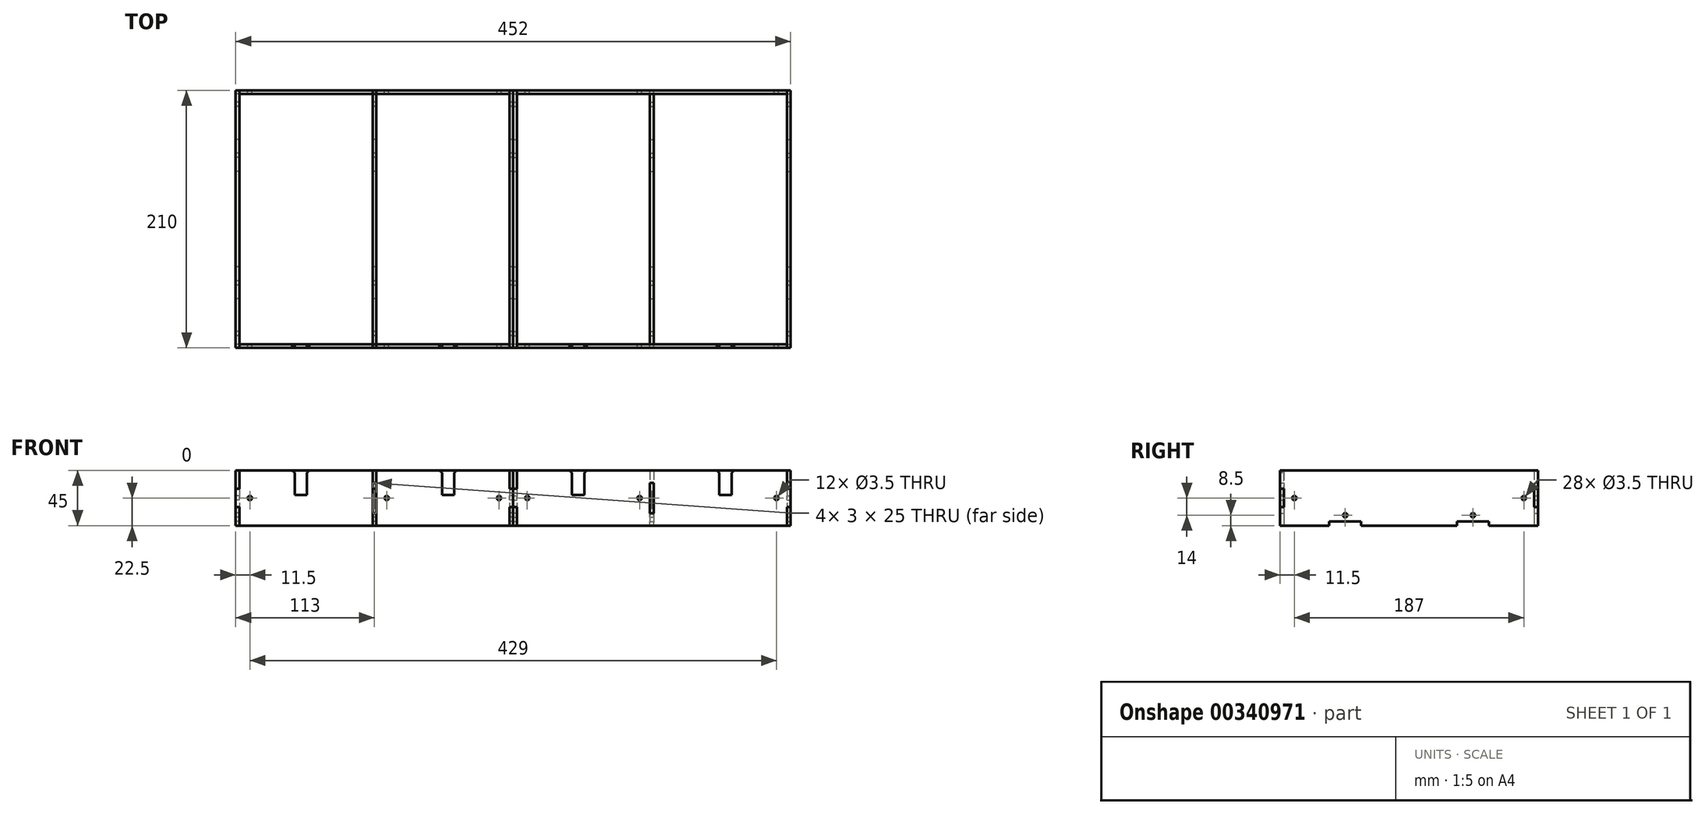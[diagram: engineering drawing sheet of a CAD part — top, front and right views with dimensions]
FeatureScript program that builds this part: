
annotation { "Feature Type Name" : "Feature", "Feature Type Description" : "" }
export const myFeature = defineFeature(function(context is Context, id is Id, definition is map)
    precondition{}
    {
        {
            var Q0;
            Q0=qCreatedBy(makeId("Right.planeOp"),FACE);
            var sketch = newSketch(context, id + "F0", { "sketchPlane" : qUnion([Q0])});
            skLineSegment(sketch, "E0.bottom", {"start": v(-105, 0) * mm, "end": v(-65, 0) * mm});
            skLineSegment(sketch, "E0.top", {"start": v(-105, 45) * mm, "end": v(105, 45) * mm});
            skLineSegment(sketch, "E0.left", {"start": v(-105, 0) * mm, "end": v(-105, 15) * mm});
            skLineSegment(sketch, "E0.right", {"start": v(105, 0) * mm, "end": v(105, 15) * mm});
            skPoint(sketch, "E0.middle", {"position": v(0, 22.5) * mm});
            skCircle(sketch, "E1", {"center": v(-93.5, 22.5) * mm, "radius": 1.75 * mm});
            skPoint(sketch, "E1.centerSnap0", {"position": v(-105, 22.5) * mm});
            skCircle(sketch, "E2", {"center": v(-52, 8.5) * mm, "radius": 1.75 * mm});
            skLineSegment(sketch, "E3.top", {"start": v(-65, 3.5) * mm, "end": v(-39, 3.5) * mm});
            skLineSegment(sketch, "E3.left", {"start": v(-65, 0) * mm, "end": v(-65, 3.5) * mm});
            skLineSegment(sketch, "E3.right", {"start": v(-39, 0) * mm, "end": v(-39, 3.5) * mm});
            skPoint(sketch, "E4", {"position": v(-52, 3.5) * mm});
            skLineSegment(sketch, "E5.bottom", {"start": v(-105, 30) * mm, "end": v(-102, 30) * mm});
            skLineSegment(sketch, "E5.top", {"start": v(-105, 15) * mm, "end": v(-102, 15) * mm});
            skLineSegment(sketch, "E5.right", {"start": v(-102, 30) * mm, "end": v(-102, 15) * mm});
            skPoint(sketch, "E5.middle", {"position": v(-103.5, 22.5) * mm});
            skLineSegment(sketch, "E6.trimOffspring", {"start": v(-105, 30) * mm, "end": v(-105, 45) * mm});
            skLineSegment(sketch, "E7.trimOffspring", {"start": v(-39, 0) * mm, "end": v(39, 0) * mm});
            skLineSegment(sketch, "E8.MirrorCS", {"start": v(39, 0) * mm, "end": v(39, 3.5) * mm});
            skLineSegment(sketch, "E9.MirrorCS", {"start": v(65, 0) * mm, "end": v(65, 3.5) * mm});
            skLineSegment(sketch, "E10.MirrorCS", {"start": v(105, 15) * mm, "end": v(102, 15) * mm});
            skLineSegment(sketch, "E11.MirrorCS", {"start": v(105, 30) * mm, "end": v(102, 30) * mm});
            skCircle(sketch, "E12.MirrorC", {"center": v(93.5, 22.5) * mm, "radius": 1.75 * mm});
            skPoint(sketch, "E13.MirrorP", {"position": v(103.5, 22.5) * mm});
            skLineSegment(sketch, "E14.MirrorCS", {"start": v(105, 0) * mm, "end": v(65, 0) * mm});
            skLineSegment(sketch, "E15.MirrorCS", {"start": v(39, 0) * mm, "end": v(-39, 0) * mm});
            skPoint(sketch, "E16.MirrorP", {"position": v(105, 22.5) * mm});
            skPoint(sketch, "E17.MirrorP", {"position": v(52, 3.5) * mm});
            skLineSegment(sketch, "E18.MirrorCS", {"start": v(105, 30) * mm, "end": v(105, 45) * mm});
            skLineSegment(sketch, "E19.MirrorCS", {"start": v(102, 30) * mm, "end": v(102, 15) * mm});
            skLineSegment(sketch, "E20.MirrorCS", {"start": v(65, 3.5) * mm, "end": v(39, 3.5) * mm});
            skCircle(sketch, "E21.MirrorC", {"center": v(52, 8.5) * mm, "radius": 1.75 * mm});
            skLineSegment(sketch, "E22.trimOffspring", {"start": v(65, 0) * mm, "end": v(105, 0) * mm});
            skLineSegment(sketch, "E23.trimOffspring", {"start": v(-65, 0) * mm, "end": v(-105, 0) * mm});
            skSolve(sketch);
        }
        {
            var Q0;
            Q0 = qSketchRegion(id + "F0", true);
            extrude(context, id + "F1", {"entities" : qUnion([Q0]), "depth" : 1.5 * mm, "hasSecondDirection" : true, "secondDirectionOppositeDirection" : true, "secondDirectionDepth" : 1.5 * mm});
        }
        {
            var Q0;
            Q0=makeQuery(id+"F1.opExtrude","SWEPT_BODY",BODY,{"disambiguationData":[OSD([sQuery(id+"F0.wireOp",EDGE,"E0.top"),sQuery(id+"F0.wireOp",EDGE,"E0.left"),sQuery(id+"F0.wireOp",EDGE,"E1"),sQuery(id+"F0.wireOp",EDGE,"E2"),sQuery(id+"F0.wireOp",EDGE,"E3.top"),sQuery(id+"F0.wireOp",EDGE,"E3.left"),sQuery(id+"F0.wireOp",EDGE,"E3.right"),sQuery(id+"F0.wireOp",EDGE,"E5.bottom"),sQuery(id+"F0.wireOp",EDGE,"E5.top"),sQuery(id+"F0.wireOp",EDGE,"E5.right"),sQuery(id+"F0.wireOp",EDGE,"E6.trimOffspring"),sQuery(id+"F0.wireOp",EDGE,"E8.MirrorCS"),sQuery(id+"F0.wireOp",EDGE,"E9.MirrorCS"),sQuery(id+"F0.wireOp",EDGE,"E10.MirrorCS"),sQuery(id+"F0.wireOp",EDGE,"E11.MirrorCS"),sQuery(id+"F0.wireOp",EDGE,"E12.MirrorC"),sQuery(id+"F0.wireOp",EDGE,"E0.right"),sQuery(id+"F0.wireOp",EDGE,"E15.MirrorCS"),sQuery(id+"F0.wireOp",EDGE,"E19.MirrorCS"),sQuery(id+"F0.wireOp",EDGE,"E20.MirrorCS"),sQuery(id+"F0.wireOp",EDGE,"E21.MirrorC"),sQuery(id+"F0.wireOp",EDGE,"E18.MirrorCS"),sQuery(id+"F0.wireOp",EDGE,"E22.trimOffspring"),sQuery(id+"F0.wireOp",EDGE,"E23.trimOffspring")])]});
            transform(context, id + "F2", {"entities" : qUnion([Q0]), "transformType" : TransformType.TRANSLATION_3D, "dx" : (223 / 2) * mm, "dy" : 0 * mm, "dz" : 0 * mm, "makeCopy" : true});
        }
        {
            var Q0;
            Q0=makeQuery(id+"F1.opExtrude","SWEPT_BODY",BODY,{"disambiguationData":[OSD([sQuery(id+"F0.wireOp",EDGE,"E0.top"),sQuery(id+"F0.wireOp",EDGE,"E0.left"),sQuery(id+"F0.wireOp",EDGE,"E1"),sQuery(id+"F0.wireOp",EDGE,"E2"),sQuery(id+"F0.wireOp",EDGE,"E3.top"),sQuery(id+"F0.wireOp",EDGE,"E3.left"),sQuery(id+"F0.wireOp",EDGE,"E3.right"),sQuery(id+"F0.wireOp",EDGE,"E5.bottom"),sQuery(id+"F0.wireOp",EDGE,"E5.top"),sQuery(id+"F0.wireOp",EDGE,"E5.right"),sQuery(id+"F0.wireOp",EDGE,"E6.trimOffspring"),sQuery(id+"F0.wireOp",EDGE,"E8.MirrorCS"),sQuery(id+"F0.wireOp",EDGE,"E9.MirrorCS"),sQuery(id+"F0.wireOp",EDGE,"E10.MirrorCS"),sQuery(id+"F0.wireOp",EDGE,"E11.MirrorCS"),sQuery(id+"F0.wireOp",EDGE,"E12.MirrorC"),sQuery(id+"F0.wireOp",EDGE,"E0.right"),sQuery(id+"F0.wireOp",EDGE,"E15.MirrorCS"),sQuery(id+"F0.wireOp",EDGE,"E19.MirrorCS"),sQuery(id+"F0.wireOp",EDGE,"E20.MirrorCS"),sQuery(id+"F0.wireOp",EDGE,"E21.MirrorC"),sQuery(id+"F0.wireOp",EDGE,"E18.MirrorCS"),sQuery(id+"F0.wireOp",EDGE,"E22.trimOffspring"),sQuery(id+"F0.wireOp",EDGE,"E23.trimOffspring")])]});
            transform(context, id + "F3", {"entities" : qUnion([Q0]), "transformType" : TransformType.TRANSLATION_3D, "dx" : (-(223 / 2)) * mm, "dy" : 0 * mm, "dz" : 0 * mm, "makeCopy" : true});
        }
        {
            var Q0;
            Q0=makeQuery(id+"F1.opExtrude","SWEPT_BODY",BODY,{"disambiguationData":[OSD([sQuery(id+"F0.wireOp",EDGE,"E0.top"),sQuery(id+"F0.wireOp",EDGE,"E0.left"),sQuery(id+"F0.wireOp",EDGE,"E1"),sQuery(id+"F0.wireOp",EDGE,"E2"),sQuery(id+"F0.wireOp",EDGE,"E3.top"),sQuery(id+"F0.wireOp",EDGE,"E3.left"),sQuery(id+"F0.wireOp",EDGE,"E3.right"),sQuery(id+"F0.wireOp",EDGE,"E5.bottom"),sQuery(id+"F0.wireOp",EDGE,"E5.top"),sQuery(id+"F0.wireOp",EDGE,"E5.right"),sQuery(id+"F0.wireOp",EDGE,"E6.trimOffspring"),sQuery(id+"F0.wireOp",EDGE,"E8.MirrorCS"),sQuery(id+"F0.wireOp",EDGE,"E9.MirrorCS"),sQuery(id+"F0.wireOp",EDGE,"E10.MirrorCS"),sQuery(id+"F0.wireOp",EDGE,"E11.MirrorCS"),sQuery(id+"F0.wireOp",EDGE,"E12.MirrorC"),sQuery(id+"F0.wireOp",EDGE,"E0.right"),sQuery(id+"F0.wireOp",EDGE,"E15.MirrorCS"),sQuery(id+"F0.wireOp",EDGE,"E19.MirrorCS"),sQuery(id+"F0.wireOp",EDGE,"E20.MirrorCS"),sQuery(id+"F0.wireOp",EDGE,"E21.MirrorC"),sQuery(id+"F0.wireOp",EDGE,"E18.MirrorCS"),sQuery(id+"F0.wireOp",EDGE,"E22.trimOffspring"),sQuery(id+"F0.wireOp",EDGE,"E23.trimOffspring")])]});
            transform(context, id + "F4", {"entities" : qUnion([Q0]), "transformType" : TransformType.TRANSLATION_3D, "dx" : 0 * mm, "dy" : 0 * mm, "dz" : 0 * mm, "makeCopy" : true});
        }
        {
            var Q0;
            Q0=makeQuery(id+"F4.opPattern","COPY",BODY,{"derivedFrom":makeQuery(id+"F1.opExtrude","SWEPT_BODY",BODY,{"disambiguationData":[OSD([sQuery(id+"F0.wireOp",EDGE,"E0.top"),sQuery(id+"F0.wireOp",EDGE,"E0.left"),sQuery(id+"F0.wireOp",EDGE,"E1"),sQuery(id+"F0.wireOp",EDGE,"E2"),sQuery(id+"F0.wireOp",EDGE,"E3.top"),sQuery(id+"F0.wireOp",EDGE,"E3.left"),sQuery(id+"F0.wireOp",EDGE,"E3.right"),sQuery(id+"F0.wireOp",EDGE,"E5.bottom"),sQuery(id+"F0.wireOp",EDGE,"E5.top"),sQuery(id+"F0.wireOp",EDGE,"E5.right"),sQuery(id+"F0.wireOp",EDGE,"E6.trimOffspring"),sQuery(id+"F0.wireOp",EDGE,"E8.MirrorCS"),sQuery(id+"F0.wireOp",EDGE,"E9.MirrorCS"),sQuery(id+"F0.wireOp",EDGE,"E10.MirrorCS"),sQuery(id+"F0.wireOp",EDGE,"E11.MirrorCS"),sQuery(id+"F0.wireOp",EDGE,"E12.MirrorC"),sQuery(id+"F0.wireOp",EDGE,"E0.right"),sQuery(id+"F0.wireOp",EDGE,"E15.MirrorCS"),sQuery(id+"F0.wireOp",EDGE,"E19.MirrorCS"),sQuery(id+"F0.wireOp",EDGE,"E20.MirrorCS"),sQuery(id+"F0.wireOp",EDGE,"E21.MirrorC"),sQuery(id+"F0.wireOp",EDGE,"E18.MirrorCS"),sQuery(id+"F0.wireOp",EDGE,"E22.trimOffspring"),sQuery(id+"F0.wireOp",EDGE,"E23.trimOffspring")])]}),"instanceName":"1"});
            deleteBodies(context, id + "F5", {"entities" : qUnion([Q0])});
        }
        {
            var Q0;
            Q0=qCreatedBy(makeId("Right.planeOp"),FACE);
            var sketch = newSketch(context, id + "F6", { "sketchPlane" : qUnion([Q0])});
            skLineSegment(sketch, "E24.bottom", {"start": v(-102, 0) * mm, "end": v(-65, 0) * mm});
            skLineSegment(sketch, "E24.top", {"start": v(-102, 45) * mm, "end": v(102, 45) * mm});
            skLineSegment(sketch, "E24.left", {"start": v(-105, 10) * mm, "end": v(-105, 35) * mm});
            skCircle(sketch, "E25", {"center": v(-93.5, 22.5) * mm, "radius": 1.75 * mm});
            skCircle(sketch, "E26", {"center": v(-52, 8.5) * mm, "radius": 1.75 * mm});
            skLineSegment(sketch, "E27.top", {"start": v(-65, 3.5) * mm, "end": v(-39, 3.5) * mm});
            skLineSegment(sketch, "E27.left", {"start": v(-65, 0) * mm, "end": v(-65, 3.5) * mm});
            skLineSegment(sketch, "E27.right", {"start": v(-39, 0) * mm, "end": v(-39, 3.5) * mm});
            skPoint(sketch, "E28", {"position": v(-52, 3.5) * mm});
            skLineSegment(sketch, "E29.trimOffspring", {"start": v(-39, 0) * mm, "end": v(39, 0) * mm});
            skLineSegment(sketch, "E30.MirrorCS", {"start": v(39, 0) * mm, "end": v(39, 3.5) * mm});
            skLineSegment(sketch, "E31.MirrorCS", {"start": v(65, 0) * mm, "end": v(65, 3.5) * mm});
            skCircle(sketch, "E32.MirrorC", {"center": v(93.5, 22.5) * mm, "radius": 1.75 * mm});
            skLineSegment(sketch, "E33.MirrorCS", {"start": v(102, 0) * mm, "end": v(65, 0) * mm});
            skLineSegment(sketch, "E34.MirrorCS", {"start": v(39, 0) * mm, "end": v(-39, 0) * mm});
            skPoint(sketch, "E35.MirrorP", {"position": v(52, 3.5) * mm});
            skLineSegment(sketch, "E36.MirrorCS", {"start": v(65, 3.5) * mm, "end": v(39, 3.5) * mm});
            skCircle(sketch, "E37.MirrorC", {"center": v(52, 8.5) * mm, "radius": 1.75 * mm});
            skLineSegment(sketch, "E38.trimOffspring", {"start": v(65, 0) * mm, "end": v(102, 0) * mm});
            skLineSegment(sketch, "E39.trimOffspring", {"start": v(-65, 0) * mm, "end": v(-102, 0) * mm});
            skLineSegment(sketch, "E40", {"start": v(-102, 45) * mm, "end": v(-102, 35) * mm});
            skLineSegment(sketch, "E41", {"start": v(-102, 35) * mm, "end": v(-105, 35) * mm});
            skLineSegment(sketch, "E42", {"start": v(-105, 10) * mm, "end": v(-102, 10) * mm});
            skLineSegment(sketch, "E43", {"start": v(-102, 10) * mm, "end": v(-102, 0) * mm});
            skLineSegment(sketch, "E44.MirrorCS", {"start": v(102, 45) * mm, "end": v(102, 35) * mm});
            skLineSegment(sketch, "E45.MirrorCS", {"start": v(102, 35) * mm, "end": v(105, 35) * mm});
            skLineSegment(sketch, "E46.MirrorCS", {"start": v(105, 35) * mm, "end": v(105, 10) * mm});
            skLineSegment(sketch, "E47.MirrorCS", {"start": v(105, 10) * mm, "end": v(102, 10) * mm});
            skLineSegment(sketch, "E48.MirrorCS", {"start": v(102, 10) * mm, "end": v(102, 0) * mm});
            skPoint(sketch, "E49", {"position": v(-105, 22.5) * mm});
            skSolve(sketch);
        }
        {
            var Q0;
            Q0 = qSketchRegion(id + "F6", true);
            extrude(context, id + "F7", {"entities" : qUnion([Q0]), "depth" : 1.5 * mm, "hasSecondDirection" : true, "secondDirectionOppositeDirection" : true, "secondDirectionDepth" : 1.5 * mm});
        }
        {
            var Q0;
            Q0=makeQuery(id+"F7.opExtrude","SWEPT_FACE",FACE,{"disambiguationData":[OSD([sQuery(id+"F6.wireOp",EDGE,"E40")])]});
            var sketch = newSketch(context, id + "F8", { "sketchPlane" : qUnion([Q0])});
            skLineSegment(sketch, "E50", {"start": v(110, 45) * mm, "end": v(-110, 45) * mm});
            skLineSegment(sketch, "E51", {"start": v(-110, 45) * mm, "end": v(-110, 30) * mm});
            skLineSegment(sketch, "E52", {"start": v(-110, 30) * mm, "end": v(-113, 30) * mm});
            skLineSegment(sketch, "E53", {"start": v(-113, 30) * mm, "end": v(-113, 15) * mm});
            skLineSegment(sketch, "E54", {"start": v(-113, 15) * mm, "end": v(-110, 15) * mm});
            skLineSegment(sketch, "E55", {"start": v(-110, 15) * mm, "end": v(-110, 0) * mm});
            skLineSegment(sketch, "E56", {"start": v(-110, 0) * mm, "end": v(110, 0) * mm});
            skLineSegment(sketch, "E57", {"start": v(110, 0) * mm, "end": v(110, 15) * mm});
            skLineSegment(sketch, "E58", {"start": v(110, 15) * mm, "end": v(113, 15) * mm});
            skLineSegment(sketch, "E59", {"start": v(113, 15) * mm, "end": v(113, 30) * mm});
            skLineSegment(sketch, "E60", {"start": v(113, 30) * mm, "end": v(110, 30) * mm});
            skLineSegment(sketch, "E61", {"start": v(110, 30) * mm, "end": v(110, 45) * mm});
            skLineSegment(sketch, "E62.bottom", {"start": v(-1.5, 35) * mm, "end": v(1.5, 35) * mm});
            skLineSegment(sketch, "E62.top", {"start": v(-1.5, 10) * mm, "end": v(1.5, 10) * mm});
            skLineSegment(sketch, "E62.left", {"start": v(-1.5, 35) * mm, "end": v(-1.5, 10) * mm});
            skLineSegment(sketch, "E62.right", {"start": v(1.5, 35) * mm, "end": v(1.5, 10) * mm});
            skPoint(sketch, "E63", {"position": v(-113, 22.5) * mm});
            skCircle(sketch, "E64", {"center": v(-101.5, 22.5) * mm, "radius": 1.75 * mm});
            skCircle(sketch, "E65", {"center": v(10, 22.5) * mm, "radius": 1.75 * mm});
            skCircle(sketch, "E66.MirrorC", {"center": v(101.5, 22.5) * mm, "radius": 1.75 * mm});
            skSolve(sketch);
        }
        {
            var Q0;
            Q0 = qSketchRegion(id + "F8", true);
            extrude(context, id + "F9", {"entities" : qUnion([Q0]), "depth" : 3 * mm});
        }
        {
            var Q0;
            Q0=makeQuery(id+"F9.opExtrude","SWEPT_BODY",BODY,{"disambiguationData":[OSD([sQuery(id+"F8.wireOp",EDGE,"E50"),sQuery(id+"F8.wireOp",EDGE,"E51"),sQuery(id+"F8.wireOp",EDGE,"E52"),sQuery(id+"F8.wireOp",EDGE,"E53"),sQuery(id+"F8.wireOp",EDGE,"E54"),sQuery(id+"F8.wireOp",EDGE,"E55"),sQuery(id+"F8.wireOp",EDGE,"E56"),sQuery(id+"F8.wireOp",EDGE,"E57"),sQuery(id+"F8.wireOp",EDGE,"E58"),sQuery(id+"F8.wireOp",EDGE,"E59"),sQuery(id+"F8.wireOp",EDGE,"E60"),sQuery(id+"F8.wireOp",EDGE,"E61"),sQuery(id+"F8.wireOp",EDGE,"E62.bottom"),sQuery(id+"F8.wireOp",EDGE,"E62.top"),sQuery(id+"F8.wireOp",EDGE,"E62.left"),sQuery(id+"F8.wireOp",EDGE,"E62.right"),sQuery(id+"F8.wireOp",EDGE,"E64"),sQuery(id+"F8.wireOp",EDGE,"E65"),sQuery(id+"F8.wireOp",EDGE,"E66.MirrorC")])]});
            transform(context, id + "F10", {"entities" : qUnion([Q0]), "transformType" : TransformType.TRANSLATION_3D, "dx" : 0 * mm, "dy" : (210 - 3) * mm, "dz" : 0 * mm, "makeCopy" : true});
        }
        {
            var Q0;
            Q0=makeQuery(id+"F9.opExtrude","CAP_FACE",FACE,{"disambiguationData":[OSD([sQuery(id+"F8.wireOp",EDGE,"E50"),sQuery(id+"F8.wireOp",EDGE,"E51"),sQuery(id+"F8.wireOp",EDGE,"E52"),sQuery(id+"F8.wireOp",EDGE,"E53"),sQuery(id+"F8.wireOp",EDGE,"E54"),sQuery(id+"F8.wireOp",EDGE,"E55"),sQuery(id+"F8.wireOp",EDGE,"E56"),sQuery(id+"F8.wireOp",EDGE,"E57"),sQuery(id+"F8.wireOp",EDGE,"E58"),sQuery(id+"F8.wireOp",EDGE,"E59"),sQuery(id+"F8.wireOp",EDGE,"E60"),sQuery(id+"F8.wireOp",EDGE,"E61"),sQuery(id+"F8.wireOp",EDGE,"E62.bottom"),sQuery(id+"F8.wireOp",EDGE,"E62.top"),sQuery(id+"F8.wireOp",EDGE,"E62.left"),sQuery(id+"F8.wireOp",EDGE,"E62.right"),sQuery(id+"F8.wireOp",EDGE,"E64"),sQuery(id+"F8.wireOp",EDGE,"E65"),sQuery(id+"F8.wireOp",EDGE,"E66.MirrorC")])],"isStart":false});
            var sketch = newSketch(context, id + "F11", { "sketchPlane" : qUnion([Q0])});
            skLineSegment(sketch, "E67.bottom", {"start": v(-65, 45) * mm, "end": v(-55, 45) * mm});
            skLineSegment(sketch, "E67.top", {"start": v(-65, 25) * mm, "end": v(-55, 25) * mm});
            skLineSegment(sketch, "E67.left", {"start": v(-65, 43) * mm, "end": v(-65, 25) * mm});
            skLineSegment(sketch, "E67.right", {"start": v(-55, 43) * mm, "end": v(-55, 25) * mm});
            skLineSegment(sketch, "E68", {"start": v(-65, 43) * mm, "end": v(-67, 45) * mm});
            skLineSegment(sketch, "E69", {"start": v(-67, 45) * mm, "end": v(-53, 45) * mm});
            skLineSegment(sketch, "E70", {"start": v(-53, 45) * mm, "end": v(-55, 43) * mm});
            skPoint(sketch, "E71", {"position": v(-60, 45) * mm});
            skLineSegment(sketch, "E72", {"start": v(-60, 45) * mm, "end": v(-60, 25) * mm, "construction": true});
            skLineSegment(sketch, "E73.MirrorCS", {"start": v(65, 45) * mm, "end": v(55, 45) * mm});
            skLineSegment(sketch, "E74.MirrorCS", {"start": v(53, 45) * mm, "end": v(55, 43) * mm});
            skLineSegment(sketch, "E75.MirrorCS", {"start": v(65, 43) * mm, "end": v(67, 45) * mm});
            skLineSegment(sketch, "E76.MirrorCS", {"start": v(67, 45) * mm, "end": v(53, 45) * mm});
            skLineSegment(sketch, "E77.MirrorCS", {"start": v(65, 25) * mm, "end": v(55, 25) * mm});
            skLineSegment(sketch, "E78.MirrorCS", {"start": v(65, 43) * mm, "end": v(65, 25) * mm});
            skPoint(sketch, "E79.MirrorP", {"position": v(60, 45) * mm});
            skLineSegment(sketch, "E80.MirrorCS", {"start": v(60, 45) * mm, "end": v(60, 25) * mm, "construction": true});
            skLineSegment(sketch, "E81.MirrorCS", {"start": v(55, 43) * mm, "end": v(55, 25) * mm});
            skSolve(sketch);
        }
        {
            var Q0;
            Q0 = qSketchRegion(id + "F11", true);
            extrude(context, id + "F12", {"entities" : qUnion([Q0]), "operationType" : NewBodyOperationType.REMOVE, "endBound" : BoundingType.UP_TO_NEXT, "oppositeDirection" : true, "depth" : 25 * mm});
        }
        {
            var Q0;
            Q0=makeQuery(id+"F2.opPattern","COPY",BODY,{"derivedFrom":makeQuery(id+"F1.opExtrude","SWEPT_BODY",BODY,{"disambiguationData":[OSD([sQuery(id+"F0.wireOp",EDGE,"E0.top"),sQuery(id+"F0.wireOp",EDGE,"E0.left"),sQuery(id+"F0.wireOp",EDGE,"E1"),sQuery(id+"F0.wireOp",EDGE,"E2"),sQuery(id+"F0.wireOp",EDGE,"E3.top"),sQuery(id+"F0.wireOp",EDGE,"E3.left"),sQuery(id+"F0.wireOp",EDGE,"E3.right"),sQuery(id+"F0.wireOp",EDGE,"E5.bottom"),sQuery(id+"F0.wireOp",EDGE,"E5.top"),sQuery(id+"F0.wireOp",EDGE,"E5.right"),sQuery(id+"F0.wireOp",EDGE,"E6.trimOffspring"),sQuery(id+"F0.wireOp",EDGE,"E8.MirrorCS"),sQuery(id+"F0.wireOp",EDGE,"E9.MirrorCS"),sQuery(id+"F0.wireOp",EDGE,"E10.MirrorCS"),sQuery(id+"F0.wireOp",EDGE,"E11.MirrorCS"),sQuery(id+"F0.wireOp",EDGE,"E12.MirrorC"),sQuery(id+"F0.wireOp",EDGE,"E0.right"),sQuery(id+"F0.wireOp",EDGE,"E15.MirrorCS"),sQuery(id+"F0.wireOp",EDGE,"E19.MirrorCS"),sQuery(id+"F0.wireOp",EDGE,"E20.MirrorCS"),sQuery(id+"F0.wireOp",EDGE,"E21.MirrorC"),sQuery(id+"F0.wireOp",EDGE,"E18.MirrorCS"),sQuery(id+"F0.wireOp",EDGE,"E22.trimOffspring"),sQuery(id+"F0.wireOp",EDGE,"E23.trimOffspring")])]}),"instanceName":"1"});
            var Q1;
            Q1=makeQuery(id+"F3.opPattern","COPY",BODY,{"derivedFrom":makeQuery(id+"F1.opExtrude","SWEPT_BODY",BODY,{"disambiguationData":[OSD([sQuery(id+"F0.wireOp",EDGE,"E0.top"),sQuery(id+"F0.wireOp",EDGE,"E0.left"),sQuery(id+"F0.wireOp",EDGE,"E1"),sQuery(id+"F0.wireOp",EDGE,"E2"),sQuery(id+"F0.wireOp",EDGE,"E3.top"),sQuery(id+"F0.wireOp",EDGE,"E3.left"),sQuery(id+"F0.wireOp",EDGE,"E3.right"),sQuery(id+"F0.wireOp",EDGE,"E5.bottom"),sQuery(id+"F0.wireOp",EDGE,"E5.top"),sQuery(id+"F0.wireOp",EDGE,"E5.right"),sQuery(id+"F0.wireOp",EDGE,"E6.trimOffspring"),sQuery(id+"F0.wireOp",EDGE,"E8.MirrorCS"),sQuery(id+"F0.wireOp",EDGE,"E9.MirrorCS"),sQuery(id+"F0.wireOp",EDGE,"E10.MirrorCS"),sQuery(id+"F0.wireOp",EDGE,"E11.MirrorCS"),sQuery(id+"F0.wireOp",EDGE,"E12.MirrorC"),sQuery(id+"F0.wireOp",EDGE,"E0.right"),sQuery(id+"F0.wireOp",EDGE,"E15.MirrorCS"),sQuery(id+"F0.wireOp",EDGE,"E19.MirrorCS"),sQuery(id+"F0.wireOp",EDGE,"E20.MirrorCS"),sQuery(id+"F0.wireOp",EDGE,"E21.MirrorC"),sQuery(id+"F0.wireOp",EDGE,"E18.MirrorCS"),sQuery(id+"F0.wireOp",EDGE,"E22.trimOffspring"),sQuery(id+"F0.wireOp",EDGE,"E23.trimOffspring")])]}),"instanceName":"1"});
            var Q2;
            Q2=makeQuery(id+"F7.opExtrude","SWEPT_BODY",BODY,{"disambiguationData":[OSD([sQuery(id+"F6.wireOp",EDGE,"E24.top"),sQuery(id+"F6.wireOp",EDGE,"E24.left"),sQuery(id+"F6.wireOp",EDGE,"E25"),sQuery(id+"F6.wireOp",EDGE,"E26"),sQuery(id+"F6.wireOp",EDGE,"E27.top"),sQuery(id+"F6.wireOp",EDGE,"E27.left"),sQuery(id+"F6.wireOp",EDGE,"E27.right"),sQuery(id+"F6.wireOp",EDGE,"E30.MirrorCS"),sQuery(id+"F6.wireOp",EDGE,"E31.MirrorCS"),sQuery(id+"F6.wireOp",EDGE,"E32.MirrorC"),sQuery(id+"F6.wireOp",EDGE,"E34.MirrorCS"),sQuery(id+"F6.wireOp",EDGE,"E36.MirrorCS"),sQuery(id+"F6.wireOp",EDGE,"E37.MirrorC"),sQuery(id+"F6.wireOp",EDGE,"E38.trimOffspring"),sQuery(id+"F6.wireOp",EDGE,"E39.trimOffspring"),sQuery(id+"F6.wireOp",EDGE,"E40"),sQuery(id+"F6.wireOp",EDGE,"E41"),sQuery(id+"F6.wireOp",EDGE,"E42"),sQuery(id+"F6.wireOp",EDGE,"E43"),sQuery(id+"F6.wireOp",EDGE,"E44.MirrorCS"),sQuery(id+"F6.wireOp",EDGE,"E45.MirrorCS"),sQuery(id+"F6.wireOp",EDGE,"E46.MirrorCS"),sQuery(id+"F6.wireOp",EDGE,"E47.MirrorCS"),sQuery(id+"F6.wireOp",EDGE,"E48.MirrorCS")])]});
            var Q3;
            Q3=makeQuery(id+"F9.opExtrude","SWEPT_BODY",BODY,{"disambiguationData":[OSD([sQuery(id+"F8.wireOp",EDGE,"E50"),sQuery(id+"F8.wireOp",EDGE,"E51"),sQuery(id+"F8.wireOp",EDGE,"E52"),sQuery(id+"F8.wireOp",EDGE,"E53"),sQuery(id+"F8.wireOp",EDGE,"E54"),sQuery(id+"F8.wireOp",EDGE,"E55"),sQuery(id+"F8.wireOp",EDGE,"E56"),sQuery(id+"F8.wireOp",EDGE,"E57"),sQuery(id+"F8.wireOp",EDGE,"E58"),sQuery(id+"F8.wireOp",EDGE,"E59"),sQuery(id+"F8.wireOp",EDGE,"E60"),sQuery(id+"F8.wireOp",EDGE,"E61"),sQuery(id+"F8.wireOp",EDGE,"E62.bottom"),sQuery(id+"F8.wireOp",EDGE,"E62.top"),sQuery(id+"F8.wireOp",EDGE,"E62.left"),sQuery(id+"F8.wireOp",EDGE,"E62.right"),sQuery(id+"F8.wireOp",EDGE,"E64"),sQuery(id+"F8.wireOp",EDGE,"E65"),sQuery(id+"F8.wireOp",EDGE,"E66.MirrorC")])]});
            var Q4;
            Q4=makeQuery(id+"F10.opPattern","COPY",BODY,{"derivedFrom":makeQuery(id+"F9.opExtrude","SWEPT_BODY",BODY,{"disambiguationData":[OSD([sQuery(id+"F8.wireOp",EDGE,"E50"),sQuery(id+"F8.wireOp",EDGE,"E51"),sQuery(id+"F8.wireOp",EDGE,"E52"),sQuery(id+"F8.wireOp",EDGE,"E53"),sQuery(id+"F8.wireOp",EDGE,"E54"),sQuery(id+"F8.wireOp",EDGE,"E55"),sQuery(id+"F8.wireOp",EDGE,"E56"),sQuery(id+"F8.wireOp",EDGE,"E57"),sQuery(id+"F8.wireOp",EDGE,"E58"),sQuery(id+"F8.wireOp",EDGE,"E59"),sQuery(id+"F8.wireOp",EDGE,"E60"),sQuery(id+"F8.wireOp",EDGE,"E61"),sQuery(id+"F8.wireOp",EDGE,"E62.bottom"),sQuery(id+"F8.wireOp",EDGE,"E62.top"),sQuery(id+"F8.wireOp",EDGE,"E62.left"),sQuery(id+"F8.wireOp",EDGE,"E62.right"),sQuery(id+"F8.wireOp",EDGE,"E64"),sQuery(id+"F8.wireOp",EDGE,"E65"),sQuery(id+"F8.wireOp",EDGE,"E66.MirrorC")])]}),"instanceName":"1"});
            var Q5;
            Q5=makeQuery(id+"F2.opPattern","COPY",FACE,{"derivedFrom":makeQuery(id+"F1.opExtrude","CAP_FACE",FACE,{"disambiguationData":[OSD([sQuery(id+"F0.wireOp",EDGE,"E0.top"),sQuery(id+"F0.wireOp",EDGE,"E0.left"),sQuery(id+"F0.wireOp",EDGE,"E1"),sQuery(id+"F0.wireOp",EDGE,"E2"),sQuery(id+"F0.wireOp",EDGE,"E3.top"),sQuery(id+"F0.wireOp",EDGE,"E3.left"),sQuery(id+"F0.wireOp",EDGE,"E3.right"),sQuery(id+"F0.wireOp",EDGE,"E5.bottom"),sQuery(id+"F0.wireOp",EDGE,"E5.top"),sQuery(id+"F0.wireOp",EDGE,"E5.right"),sQuery(id+"F0.wireOp",EDGE,"E6.trimOffspring"),sQuery(id+"F0.wireOp",EDGE,"E8.MirrorCS"),sQuery(id+"F0.wireOp",EDGE,"E9.MirrorCS"),sQuery(id+"F0.wireOp",EDGE,"E10.MirrorCS"),sQuery(id+"F0.wireOp",EDGE,"E11.MirrorCS"),sQuery(id+"F0.wireOp",EDGE,"E12.MirrorC"),sQuery(id+"F0.wireOp",EDGE,"E0.right"),sQuery(id+"F0.wireOp",EDGE,"E15.MirrorCS"),sQuery(id+"F0.wireOp",EDGE,"E19.MirrorCS"),sQuery(id+"F0.wireOp",EDGE,"E20.MirrorCS"),sQuery(id+"F0.wireOp",EDGE,"E21.MirrorC"),sQuery(id+"F0.wireOp",EDGE,"E18.MirrorCS"),sQuery(id+"F0.wireOp",EDGE,"E22.trimOffspring"),sQuery(id+"F0.wireOp",EDGE,"E23.trimOffspring")])],"isStart":false}),"instanceName":"1"});
            mirror(context, id + "F13", {"entities" : qUnion([Q0, Q1, Q2, Q3, Q4]), "mirrorPlane" : qUnion([Q5])});
        }
    });
